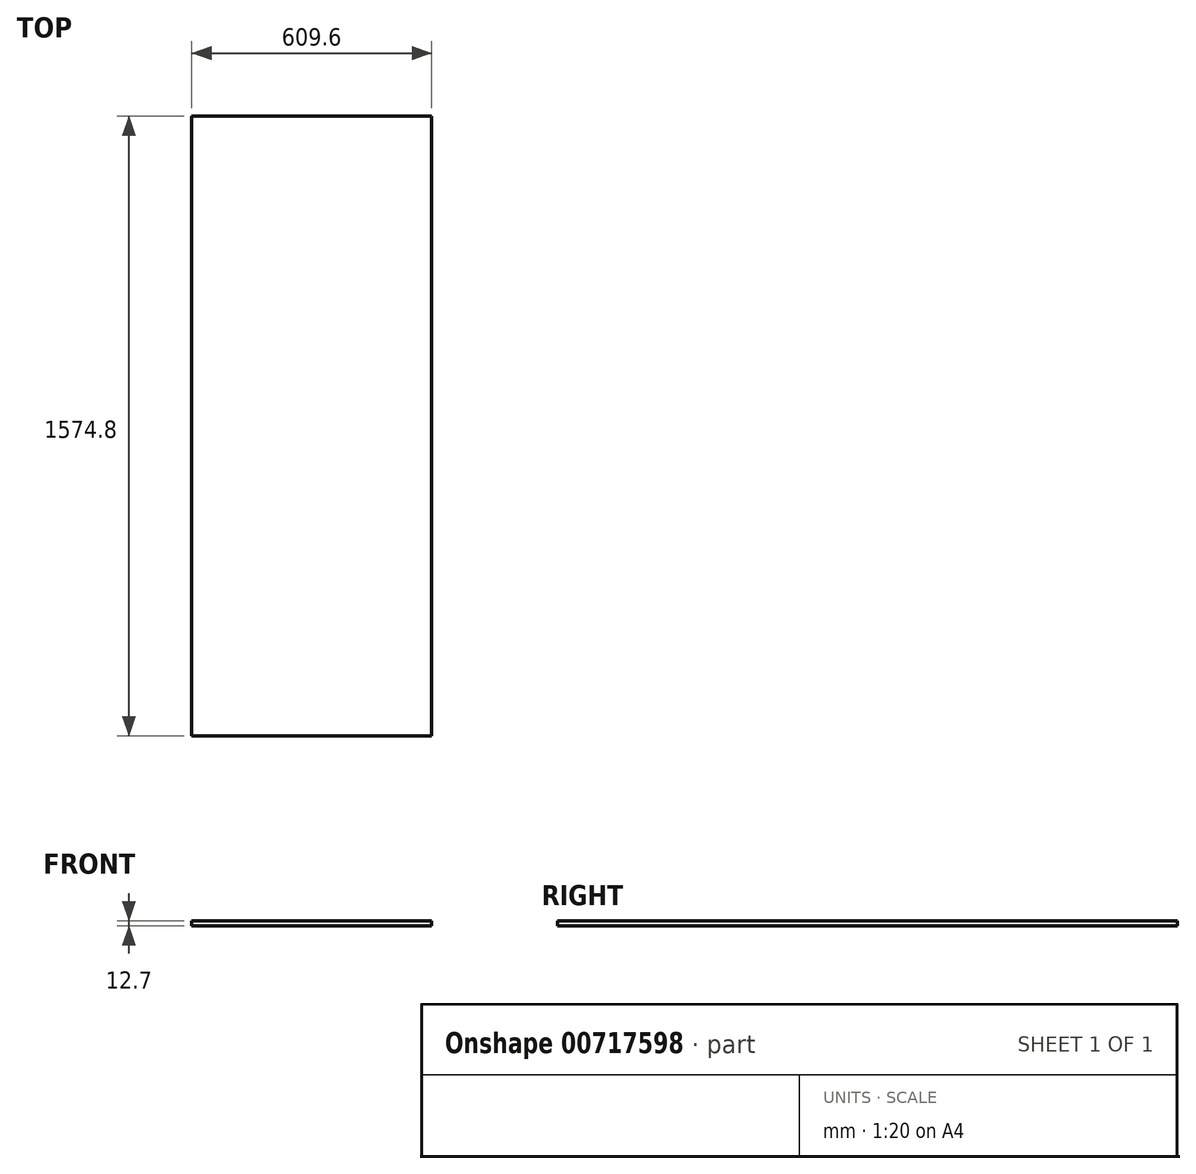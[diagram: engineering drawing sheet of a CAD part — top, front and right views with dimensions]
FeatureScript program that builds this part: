
annotation { "Feature Type Name" : "Feature", "Feature Type Description" : "" }
export const myFeature = defineFeature(function(context is Context, id is Id, definition is map)
    precondition{}
    {
        {
            var Q0;
            Q0=qCreatedBy(makeId("Top.planeOp"),FACE);
            var sketch = newSketch(context, id + "F0", { "sketchPlane" : qUnion([Q0])});
            skLineSegment(sketch, "E0.bottom", {"start": v(-304.8, -787.4) * mm, "end": v(304.8, -787.4) * mm});
            skLineSegment(sketch, "E0.top", {"start": v(-304.8, 787.4) * mm, "end": v(304.8, 787.4) * mm});
            skLineSegment(sketch, "E0.left", {"start": v(-304.8, -787.4) * mm, "end": v(-304.8, 787.4) * mm});
            skLineSegment(sketch, "E0.right", {"start": v(304.8, -787.4) * mm, "end": v(304.8, 787.4) * mm});
            skPoint(sketch, "E0.middle", {"position": v(0, 0) * mm});
            skSolve(sketch);
        }
        {
            var Q0;
            Q0=qSketchRegion(id+"F0",true);
            extrude(context, id + "F1", {"entities" : qUnion([Q0]), "depth" : 12.7 * mm, "offsetDistance" : 25.4 * mm});
        }
    });
